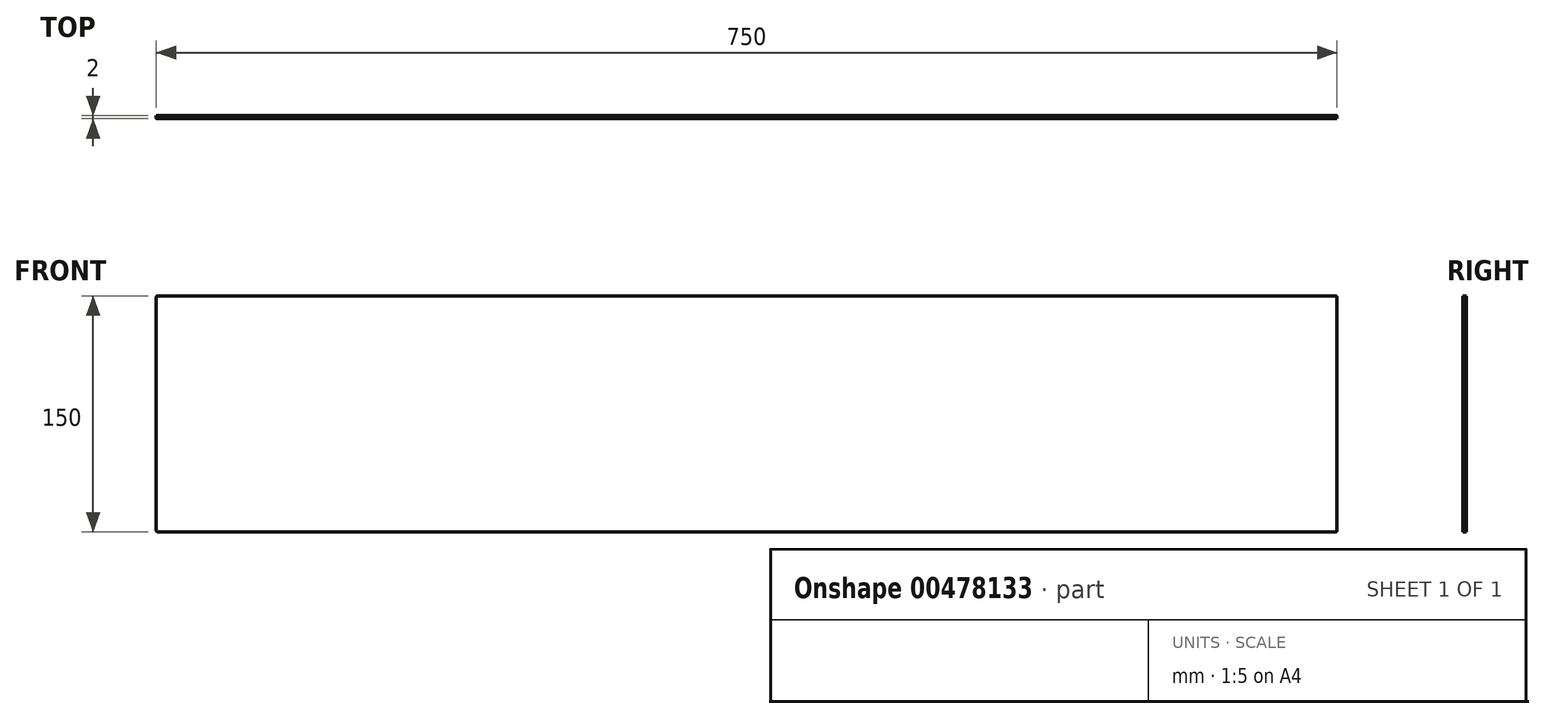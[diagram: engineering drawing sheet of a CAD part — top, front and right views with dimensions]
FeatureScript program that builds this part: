
annotation { "Feature Type Name" : "Feature", "Feature Type Description" : "" }
export const myFeature = defineFeature(function(context is Context, id is Id, definition is map)
    precondition{}
    {
        {
            var Q0;
            Q0=qCreatedBy(makeId("Front.planeOp"),FACE);
            var sketch = newSketch(context, id + "F0", { "sketchPlane" : qUnion([Q0])});
            skLineSegment(sketch, "E0.bottom", {"start": v(-375, 75) * mm, "end": v(375, 75) * mm});
            skLineSegment(sketch, "E0.top", {"start": v(-375, -75) * mm, "end": v(375, -75) * mm});
            skLineSegment(sketch, "E0.left", {"start": v(-375, 75) * mm, "end": v(-375, -75) * mm});
            skLineSegment(sketch, "E0.right", {"start": v(375, 75) * mm, "end": v(375, -75) * mm});
            skPoint(sketch, "E1.oppositeSnap0", {"position": v(0, 75) * mm});
            skLineSegment(sketch, "E2", {"start": v(-72.97, 0) * mm, "end": v(73.63, 0) * mm, "construction": true});
            skLineSegment(sketch, "E3", {"start": v(0, 70.28) * mm, "end": v(0, -60.49) * mm, "construction": true});
            skSolve(sketch);
        }
        {
            var Q0;
            Q0 = qSketchRegion(id + "F0", true);
            extrude(context, id + "F1", {"entities" : qUnion([Q0]), "depth" : 2 * mm});
        }
        {
            var Q0;
            Q0=makeQuery(id+"F1.opExtrude","SWEPT_EDGE",EDGE,{"disambiguationData":[OSD([sQuery(id+"F0.wireOp",EDGE,"E0.bottom"),sQuery(id+"F0.wireOp",EDGE,"E0.right")])]});
            var Q1;
            Q1=makeQuery(id+"F1.opExtrude","SWEPT_EDGE",EDGE,{"disambiguationData":[OSD([sQuery(id+"F0.wireOp",EDGE,"E0.top"),sQuery(id+"F0.wireOp",EDGE,"E0.right")])]});
            var Q2;
            Q2=makeQuery(id+"F1.opExtrude","SWEPT_EDGE",EDGE,{"disambiguationData":[OSD([sQuery(id+"F0.wireOp",EDGE,"E0.top"),sQuery(id+"F0.wireOp",EDGE,"E0.left")])]});
            var Q3;
            Q3=makeQuery(id+"F1.opExtrude","SWEPT_EDGE",EDGE,{"disambiguationData":[OSD([sQuery(id+"F0.wireOp",EDGE,"E0.bottom"),sQuery(id+"F0.wireOp",EDGE,"E0.left")])]});
            fillet(context, id + "F2", {"entities" : qUnion([Q0, Q1, Q2, Q3]), "radius" : 1 * mm, "tangentPropagation" : true, "allowEdgeOverflow" : false});
        }
    });
